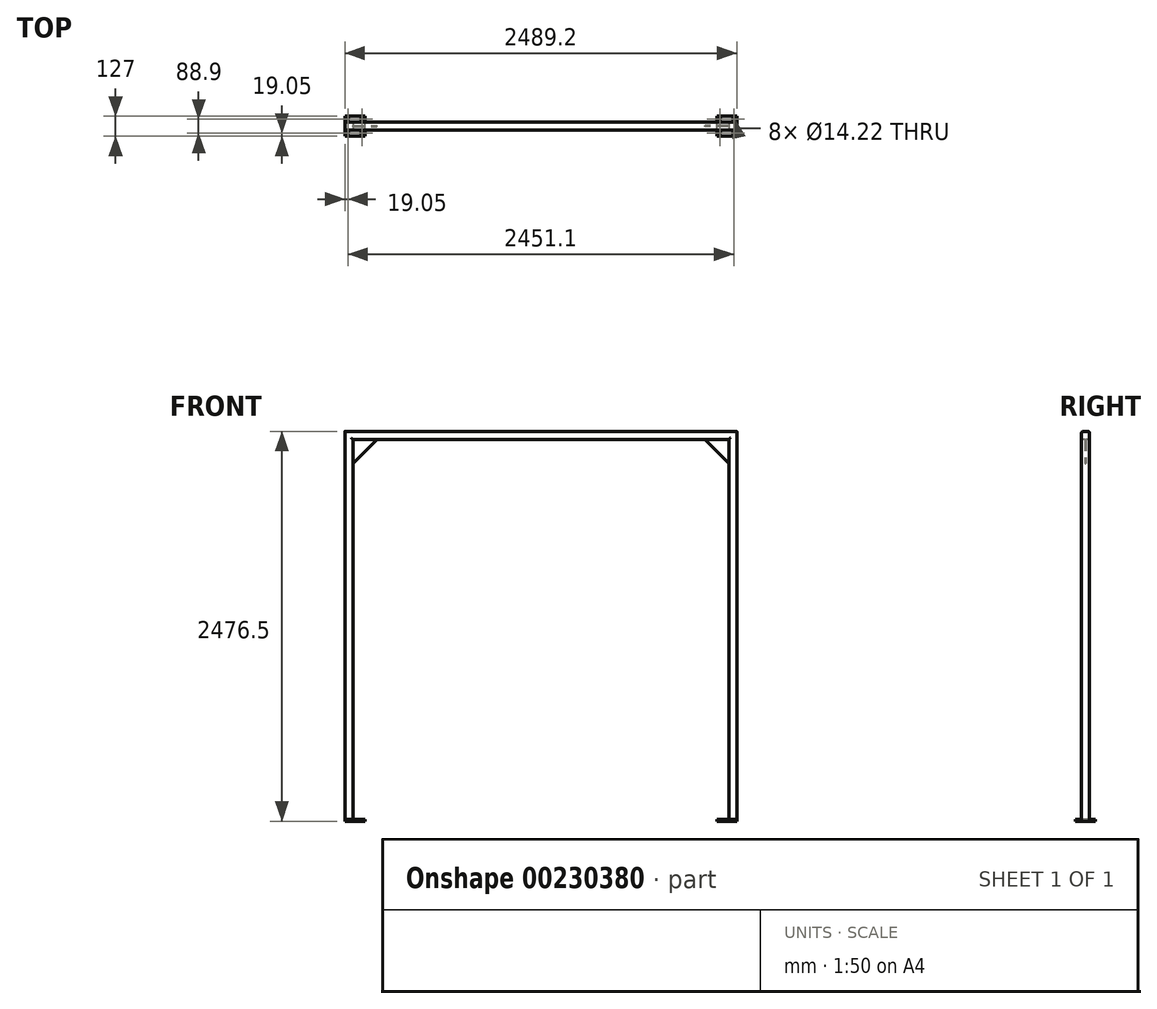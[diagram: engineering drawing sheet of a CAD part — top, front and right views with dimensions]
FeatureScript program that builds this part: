
annotation { "Feature Type Name" : "Feature", "Feature Type Description" : "" }
export const myFeature = defineFeature(function(context is Context, id is Id, definition is map)
    precondition{}
    {
        {
            var Q0;
            Q0=qCreatedBy(makeId("Front.planeOp"),FACE);
            var sketch = newSketch(context, id + "F0", { "sketchPlane" : qUnion([Q0])});
            skLineSegment(sketch, "E0", {"start": v(0, 0) * mm, "end": v(0, 2438.4) * mm});
            skLineSegment(sketch, "E1", {"start": v(0, 2438.4) * mm, "end": v(2438.4, 2438.4) * mm});
            skLineSegment(sketch, "E2", {"start": v(2438.4, 2438.4) * mm, "end": v(2438.4, 0) * mm});
            skSolve(sketch);
        }
        {
            var Q0;
            Q0=qCreatedBy(makeId("Top.planeOp"),FACE);
            var sketch = newSketch(context, id + "F1", { "sketchPlane" : qUnion([Q0])});
            skLineSegment(sketch, "E3.bottom", {"start": v(-15.88, 25.4) * mm, "end": v(15.88, 25.4) * mm});
            skLineSegment(sketch, "E3.top", {"start": v(-15.88, -25.4) * mm, "end": v(15.88, -25.4) * mm});
            skLineSegment(sketch, "E3.left", {"start": v(-25.4, 15.88) * mm, "end": v(-25.4, -15.87) * mm});
            skLineSegment(sketch, "E3.right", {"start": v(25.4, 15.88) * mm, "end": v(25.4, -15.88) * mm});
            skPoint(sketch, "E3.middle", {"position": v(0, 0) * mm});
            skPoint(sketch, "E4.visualSharp", {"position": v(-25.4, 25.4) * mm});
            skArc(sketch, "E4.filletArc", {"start": v(-15.88, 25.4) * mm, "mid": v(-22.61, 22.61) * mm, "end": v(-25.4, 15.88) * mm});
            skPoint(sketch, "E5.visualSharp", {"position": v(-25.4, -25.4) * mm});
            skArc(sketch, "E5.filletArc", {"start": v(-25.4, -15.87) * mm, "mid": v(-22.61, -22.61) * mm, "end": v(-15.88, -25.4) * mm});
            skPoint(sketch, "E6.visualSharp", {"position": v(25.4, 25.4) * mm});
            skArc(sketch, "E6.filletArc", {"start": v(25.4, 15.88) * mm, "mid": v(22.61, 22.61) * mm, "end": v(15.88, 25.4) * mm});
            skPoint(sketch, "E7.visualSharp", {"position": v(25.4, -25.4) * mm});
            skArc(sketch, "E7.filletArc", {"start": v(15.88, -25.4) * mm, "mid": v(22.61, -22.61) * mm, "end": v(25.4, -15.88) * mm});
            skSolve(sketch);
        }
        {
            var Q0;
            Q0=makeQuery(id+"F1.imprint","IMPRINT",FACE,{"disambiguationData":[TD([[makeQuery(id+"F1.imprint","IMPRINT",EDGE,{"derivedFrom":sQuery(id+"F1.wireOp",EDGE,"E3.bottom")}),-1.0]])]});
            var Q1;
            Q1=sQuery(id+"F0.wireOp",EDGE,"E0");
            var Q2;
            Q2=sQuery(id+"F0.wireOp",EDGE,"E1");
            var Q3;
            Q3=sQuery(id+"F0.wireOp",EDGE,"E2");
            sweep(context, id + "F2", {"profiles" : qUnion([Q0]), "path" : qUnion([Q1, Q2, Q3])});
        }
        {
            var Q0;
            Q0=qCreatedBy(makeId("Top.planeOp"),FACE);
            var sketch = newSketch(context, id + "F3", { "sketchPlane" : qUnion([Q0])});
            skLineSegment(sketch, "E8.0", {"start": v(-25.4, 15.88) * mm, "end": v(-25.4, -15.87) * mm, "construction": true});
            skLineSegment(sketch, "E9", {"start": v(-25.4, 0) * mm, "end": v(38.1, 0) * mm, "construction": true});
            skLineSegment(sketch, "E10.bottom", {"start": v(-25.4, -63.5) * mm, "end": v(101.6, -63.5) * mm});
            skLineSegment(sketch, "E10.top", {"start": v(-25.4, 63.5) * mm, "end": v(101.6, 63.5) * mm});
            skLineSegment(sketch, "E10.left", {"start": v(-25.4, -63.5) * mm, "end": v(-25.4, 63.5) * mm});
            skLineSegment(sketch, "E10.right", {"start": v(101.6, -63.5) * mm, "end": v(101.6, 63.5) * mm});
            skPoint(sketch, "E10.middle", {"position": v(38.1, 0) * mm});
            skLineSegment(sketch, "E11.0", {"start": v(-6.35, -44.45) * mm, "end": v(82.55, -44.45) * mm, "construction": true});
            skLineSegment(sketch, "E11.1", {"start": v(-6.35, -44.45) * mm, "end": v(-6.35, 44.45) * mm, "construction": true});
            skLineSegment(sketch, "E11.2", {"start": v(-6.35, 44.45) * mm, "end": v(82.55, 44.45) * mm, "construction": true});
            skLineSegment(sketch, "E11.3", {"start": v(82.55, -44.45) * mm, "end": v(82.55, 44.45) * mm, "construction": true});
            skCircle(sketch, "E12", {"center": v(-6.35, -44.45) * mm, "radius": 7.11 * mm});
            skCircle(sketch, "E13.0.1.0", {"center": v(-6.35, 44.45) * mm, "radius": 7.11 * mm});
            skCircle(sketch, "E13.1.0.0", {"center": v(82.55, -44.45) * mm, "radius": 7.11 * mm});
            skCircle(sketch, "E13.1.1.0", {"center": v(82.55, 44.45) * mm, "radius": 7.11 * mm});
            skLineSegment(sketch, "E14.1.0.0", {"start": v(2336.8, 63.5) * mm, "end": v(2463.8, 63.5) * mm});
            skLineSegment(sketch, "E14.1.0.1", {"start": v(2463.8, -63.5) * mm, "end": v(2463.8, 63.5) * mm});
            skLineSegment(sketch, "E14.1.0.2", {"start": v(2444.75, -44.45) * mm, "end": v(2444.75, 44.45) * mm, "construction": true});
            skPoint(sketch, "E14.1.0.3", {"position": v(2400.3, 0) * mm});
            skLineSegment(sketch, "E14.1.0.4", {"start": v(2336.8, -63.5) * mm, "end": v(2463.8, -63.5) * mm});
            skLineSegment(sketch, "E14.1.0.5", {"start": v(2355.85, 44.45) * mm, "end": v(2444.75, 44.45) * mm, "construction": true});
            skLineSegment(sketch, "E14.1.0.6", {"start": v(2355.85, -44.45) * mm, "end": v(2444.75, -44.45) * mm, "construction": true});
            skLineSegment(sketch, "E14.1.0.7", {"start": v(2336.8, 0) * mm, "end": v(2400.3, 0) * mm, "construction": true});
            skLineSegment(sketch, "E14.1.0.8", {"start": v(2355.85, -44.45) * mm, "end": v(2444.75, -44.45) * mm, "construction": true});
            skLineSegment(sketch, "E14.1.0.9", {"start": v(2336.8, 15.88) * mm, "end": v(2336.8, -15.87) * mm, "construction": true});
            skCircle(sketch, "E14.1.0.10", {"center": v(2444.75, 44.45) * mm, "radius": 7.11 * mm});
            skLineSegment(sketch, "E14.1.0.11", {"start": v(2355.85, -44.45) * mm, "end": v(2355.85, 44.45) * mm, "construction": true});
            skLineSegment(sketch, "E14.1.0.12", {"start": v(2336.8, -63.5) * mm, "end": v(2336.8, 63.5) * mm});
            skLineSegment(sketch, "E14.1.0.13", {"start": v(2355.85, -44.45) * mm, "end": v(2355.85, 44.45) * mm, "construction": true});
            skCircle(sketch, "E14.1.0.14", {"center": v(2355.85, 44.45) * mm, "radius": 7.11 * mm});
            skCircle(sketch, "E14.1.0.15", {"center": v(2444.75, -44.45) * mm, "radius": 7.11 * mm});
            skCircle(sketch, "E14.1.0.16", {"center": v(2355.85, -44.45) * mm, "radius": 7.11 * mm});
            skLineSegment(sketch, "E14.direction1", {"start": v(-25.4, -63.5) * mm, "end": v(2336.8, -63.5) * mm, "construction": true});
            skSolve(sketch);
        }
        {
            var Q0;
            Q0=qSketchRegion(id+"F3",true);
            extrude(context, id + "F4", {"entities" : qUnion([Q0]), "operationType" : NewBodyOperationType.ADD, "oppositeDirection" : true, "depth" : 12.7 * mm});
        }
        {
            var Q0;
            Q0=qCreatedBy(makeId("Front.planeOp"),FACE);
            var sketch = newSketch(context, id + "F5", { "sketchPlane" : qUnion([Q0])});
            skLineSegment(sketch, "E15.0", {"start": v(25.4, 2413) * mm, "end": v(2413, 2413) * mm, "construction": true});
            skLineSegment(sketch, "E16.0", {"start": v(25.4, 0) * mm, "end": v(25.4, 2413) * mm, "construction": true});
            skLineSegment(sketch, "E17.0", {"start": v(2413, 2413) * mm, "end": v(2413, 0) * mm, "construction": true});
            skLineSegment(sketch, "E18.bottom", {"start": v(25.4, 2413) * mm, "end": v(177.8, 2413) * mm});
            skLineSegment(sketch, "E18.top", {"start": v(25.4, 2260.6) * mm, "end": v(177.8, 2260.6) * mm});
            skLineSegment(sketch, "E18.left", {"start": v(25.4, 2413) * mm, "end": v(25.4, 2260.6) * mm});
            skLineSegment(sketch, "E19", {"start": v(25.4, 2260.6) * mm, "end": v(177.8, 2413) * mm});
            skLineSegment(sketch, "E20", {"start": v(1219.2, 2413) * mm, "end": v(1219.2, 1962.66) * mm, "construction": true});
            skLineSegment(sketch, "E21.MirrorCS", {"start": v(2413, 2413) * mm, "end": v(2260.6, 2413) * mm});
            skLineSegment(sketch, "E22.MirrorCS", {"start": v(2413, 2260.6) * mm, "end": v(2260.6, 2260.6) * mm});
            skLineSegment(sketch, "E23.MirrorCS", {"start": v(2413, 2260.6) * mm, "end": v(2260.6, 2413) * mm});
            skLineSegment(sketch, "E24.MirrorCS", {"start": v(2413, 2413) * mm, "end": v(2413, 2260.6) * mm});
            skSolve(sketch);
        }
        {
            var Q0;
            Q0=makeQuery(id+"F5.imprint","IMPRINT",FACE,{"disambiguationData":[TD([[makeQuery(id+"F5.imprint","IMPRINT",EDGE,{"derivedFrom":sQuery(id+"F5.wireOp",EDGE,"E18.bottom")}),-1.0]])]});
            var Q1;
            Q1=makeQuery(id+"F5.imprint","IMPRINT",FACE,{"disambiguationData":[TD([[makeQuery(id+"F5.imprint","IMPRINT",EDGE,{"derivedFrom":sQuery(id+"F5.wireOp",EDGE,"E21.MirrorCS")}),1.0]])]});
            extrude(context, id + "F6", {"entities" : qUnion([Q0, Q1]), "operationType" : NewBodyOperationType.ADD, "endBound" : BoundingType.SYMMETRIC, "depth" : 6.35 * mm});
        }
    });
